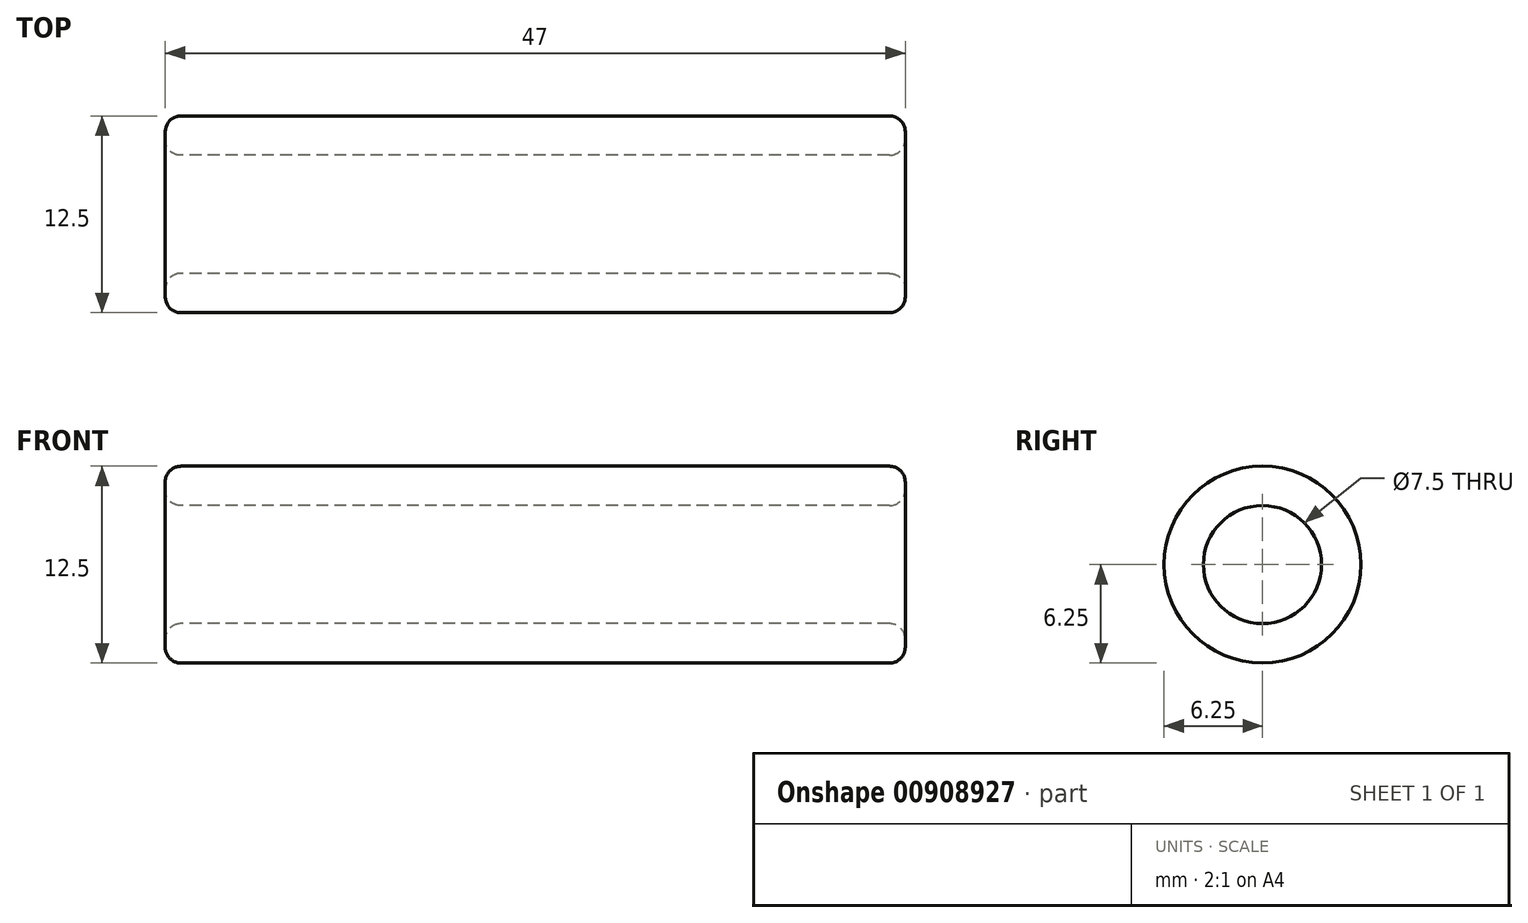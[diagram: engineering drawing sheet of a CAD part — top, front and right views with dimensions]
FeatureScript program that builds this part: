
annotation { "Feature Type Name" : "Feature", "Feature Type Description" : "" }
export const myFeature = defineFeature(function(context is Context, id is Id, definition is map)
    precondition{}
    {
        {
            var Q0;
            Q0=qCreatedBy(makeId("Right.planeOp"),FACE);
            var sketch = newSketch(context, id + "F0", { "sketchPlane" : qUnion([Q0])});
            skCircle(sketch, "E0", {"center": v(0, 0) * mm, "radius": 6.25 * mm});
            skCircle(sketch, "E1", {"center": v(0, 0) * mm, "radius": 3.75 * mm});
            skSolve(sketch);
        }
        {
            var Q0;
            Q0 = qSketchRegion(id + "F0", true);
            extrude(context, id + "F1", {"entities" : qUnion([Q0]), "depth" : 47 * mm, "offsetDistance" : 25 * mm});
        }
        {
            var Q0;
            Q0=makeQuery(id+"F1.opExtrude","CAP_FACE",FACE,{"disambiguationData":[OSD([sQuery(id+"F0.wireOp",EDGE,"E0"),sQuery(id+"F0.wireOp",EDGE,"E1")])],"isStart":true});
            var Q1;
            Q1=makeQuery(id+"F1.opExtrude","CAP_FACE",FACE,{"disambiguationData":[OSD([sQuery(id+"F0.wireOp",EDGE,"E0"),sQuery(id+"F0.wireOp",EDGE,"E1")])],"isStart":false});
            fillet(context, id + "F2", {"entities" : qUnion([Q0, Q1]), "radius" : 1 * mm, "tangentPropagation" : true, "allowEdgeOverflow" : false});
        }
    });
